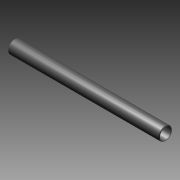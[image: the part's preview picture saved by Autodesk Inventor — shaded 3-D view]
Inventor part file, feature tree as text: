
AUTODESK INVENTOR PART (.ipt)
format: ipt  version: 2011 SP1 (Build 150282100, 282)  size: 116,224 bytes
history: native  units: in
note: dims shown in document units (in); Inventor stores cm internally (conversion verified against a paired STEP export)
features: other x42, revolve x1, sketch x1
ambient origin geometry x8: Origin, YZ Plane, XZ Plane, XY Plane, X Axis, Y Axis, Z Axis, Center Point
bodies: Solid1 (feature_tree)
feature tree (44):
  revolve  "Revolution1"  [1 undecoded]
  other  "cp1_XY"
  other  "cp1_YZ"
  other  "cp1_ZX"
  other  "cp1_X"
  other  "cp1_Y"
  other  "cp1_Z"
  other  "cp1_Center"
  other  "cp2_XY"
  other  "cp2_YZ"
  other  "cp2_ZX"
  other  "cp2_X"
  other  "cp2_Y"
  other  "cp2_Z"
  other  "cp2_Center"
  other  "cp3_XY"
  other  "cp3_YZ"
  other  "cp3_ZX"
  other  "cp3_X"
  other  "cp3_Y"
  other  "cp3_Z"
  other  "cp3_Center"
  other  "cp4_XY"
  other  "cp4_YZ"
  other  "cp4_ZX"
  other  "cp4_X"
  other  "cp4_Y"
  other  "cp4_Z"
  other  "cp4_Center"
  other  "tube_front_XY"
  other  "tube_front_YZ"
  other  "tube_front_ZX"
  other  "tube_front_X"
  other  "tube_front_Y"
  other  "tube_front_Z"
  other  "tube_front_Center"
  other  "tube_rear_XY"
  other  "tube_rear_YZ"
  other  "tube_rear_ZX"
  other  "tube_rear_X"
  other  "tube_rear_Y"
  other  "tube_rear_Z"
  other  "tube_rear_Center"
  sketch  "Sketch_1"  dims[d0=360.0deg]
note: 1 required parameter value undecoded (feature->parameter linkage not recoverable at this tier; creation-order binding heuristic only, values carry confidence <= 0.55)
